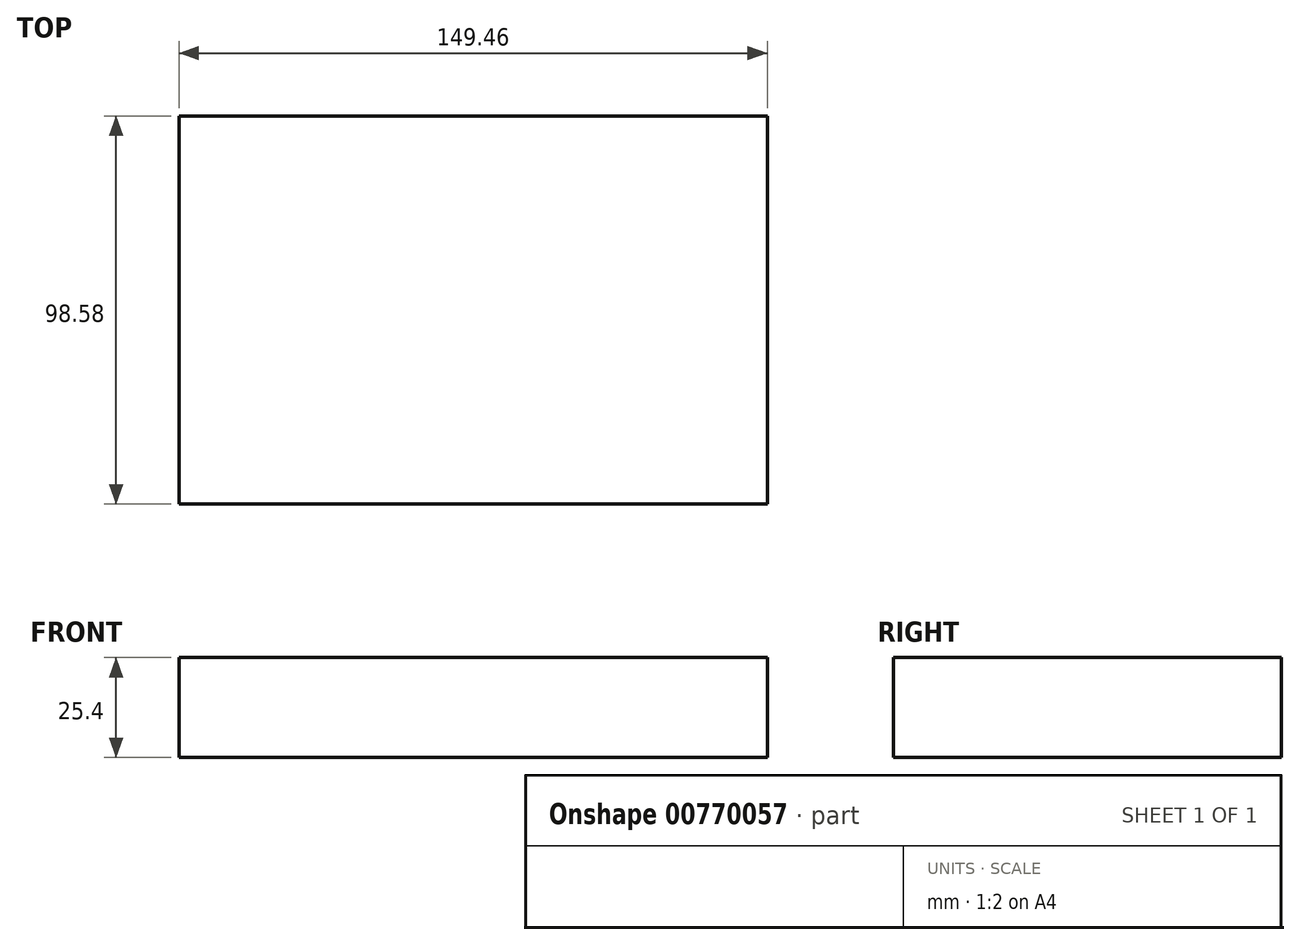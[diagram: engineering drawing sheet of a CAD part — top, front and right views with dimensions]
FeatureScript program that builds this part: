
annotation { "Feature Type Name" : "Feature", "Feature Type Description" : "" }
export const myFeature = defineFeature(function(context is Context, id is Id, definition is map)
    precondition{}
    {
        {
            var Q0;
            Q0=qCreatedBy(makeId("Top.planeOp"),FACE);
            var sketch = newSketch(context, id + "F0", { "sketchPlane" : qUnion([Q0])});
            skLineSegment(sketch, "E0.bottom", {"start": v(44.2, 39.44) * mm, "end": v(-105.26, 39.44) * mm});
            skLineSegment(sketch, "E0.top", {"start": v(44.2, -59.14) * mm, "end": v(-105.26, -59.14) * mm});
            skLineSegment(sketch, "E0.left", {"start": v(44.2, 39.44) * mm, "end": v(44.2, -59.14) * mm});
            skLineSegment(sketch, "E0.right", {"start": v(-105.26, 39.44) * mm, "end": v(-105.26, -59.14) * mm});
            skSolve(sketch);
        }
        {
            var Q0;
            Q0=makeQuery(id+"F0.imprint","IMPRINT",FACE,{"disambiguationData":[TD([[makeQuery(id+"F0.imprint","IMPRINT",EDGE,{"derivedFrom":sQuery(id+"F0.wireOp",EDGE,"E0.bottom")}),1.0]])]});
            extrude(context, id + "F1", {"entities" : qUnion([Q0]), "depth" : 25.4 * mm, "offsetDistance" : 25.4 * mm});
        }
    });
